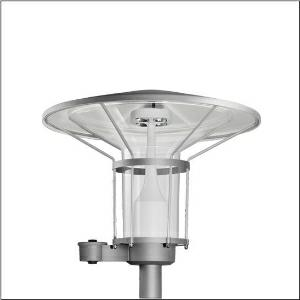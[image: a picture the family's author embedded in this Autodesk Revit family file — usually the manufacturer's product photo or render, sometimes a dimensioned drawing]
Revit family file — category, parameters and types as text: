
# Revit family: laterne_classic_iq___st1_2a_5xa5245ey14h000022_9375
name_source: partatom
category: Lighting Fixtures
units: mm (PartAtom-declared; Revit-internal decimal feet)

## family parameters
Cut with Voids When Loaded = No
Host = Face
Light Source = No
Part Type = Normal
Room Calculation Point = No
Round Connector Dimension = Use Diameter
Shared = No

## types (1)
- --- (1 x LED, 1370 lm, 10.7 W, 3000K)
    Apparent Load = 11 VA
    CIE Flux Codes = 21 60 93 97 100
    Color Rendering = 70
    Color Temperature = 3000K
    Default Elevation = 1800 mm
    Description = Lantern Classic iQ, mast luminaire, Module 540 iQ-SR, primary light control with 3 zone facetted reflector, of plastic, silver coated, highly specular, structured, primary optical cover: cover, of PMMA, transparent, light distribution: ST1.2a, light emission: direct distribution, primary light characteristic: asymmetric, installation type: post-top, LED, High Power LED, rated luminous flux: 1.370lm, luminous efficacy: 128lm/W, light colour: 730, colour temperature: 3000K, control gear: iQ-Street Remote, D4i with power reduction, control: optimised constant luminous flux control (CLO 2.0), Desk-Remote (wireless, voltage-free reading and setting of iQ features in the workshop via application-optimized NFC function/RFID function), Light-Fading, Smart-Wire, Night-Set, Lumen-Switch, Temp-Guard, Auto-Match, Street-Remote, pre-setting: logarithmic dimming characteristic, with terminal, 6-pole, max. 2.5mm², mains connection: 230..240V, AC, 50/60Hz, connection cable pre-assembled, cable length: 5,5m, wiring characteristics: H07RN-F, start of lifetime: 11W, end of service life: 11W, reduction: 6W, luminaire housing, upper part, of glass-fibre reinforced polyester, coated, Siteco® metallic grey (DB 702S), diameter: 750mm, height: 596mm, spigot size: d x l = 76 x 70mm (post-top) | with reducer (optional accessory) 60 x 70mm, mounting height: 3..5m, post-top mast mounting element, of diecast aluminium, coated, Siteco® metallic grey (DB 702S), Module 540 iQ-SR, traffic white (RAL 9016), equipment: standard, Smart Interface below and above, protection rating (complete): IP65, insulation class (complete): insulation class II (safety insulation), certification: CE, ENEC, VDE, packaging unit: 1 piece

Light Distribution: ST1.2a
    Height = 596 mm
    Lamp = 1 x LED
    Lamp Light Flux = 1370 lm
    Lamp Power = 10.7 W
    Lamp count = 1
    Length = 750 mm
    Luminous efficacy = 128 lm/W
    Manufacturer = Siteco
    ModVariant = No
    Model = 5XA5245EY14H000022
    Number of Poles = 1
    OnlyDefault = Yes
    Power Factor = 1
    Product Name = Laterne Classic iQ | ST1.2a
    Product group = mast luminaire | pylon top
    ProductGroupID = 6100
    Protection Class = Protection class II
    Protection Degree = IP 65
    RLX_Detail_Level = 1
    RLX_Emergency_Light_Flux = 0 lm
    RLX_Emergency_Type = 0
    RLX_Emergency_Type_DB = No
    RlxData = <blob elided: 63441 chars, md5=9c5778d0>
    Socket = socket
    Standby Power = 0 W
    System Light Flux = 1370 lm
    System Power = 11 W
    Type Comments = factory setting: luminous flux: 100 % | dim-lin: 254 | 419 mA
    Type Image = l_1006522.jpg
    URL = http://relux.com
    VarID = @adj_086568
    Voltage = 0 V
    Weight = 0.00 kg
    Width = 0 mm  [stored 0 ft]

note: [stored X ft] marks values corroborated as IEEE doubles in the binary element streams (Revit-internal decimal feet)

## geometry (parser evidence)
native form markers: Blend x4, Sweep x9
no freeform markers — native parametric forms only
